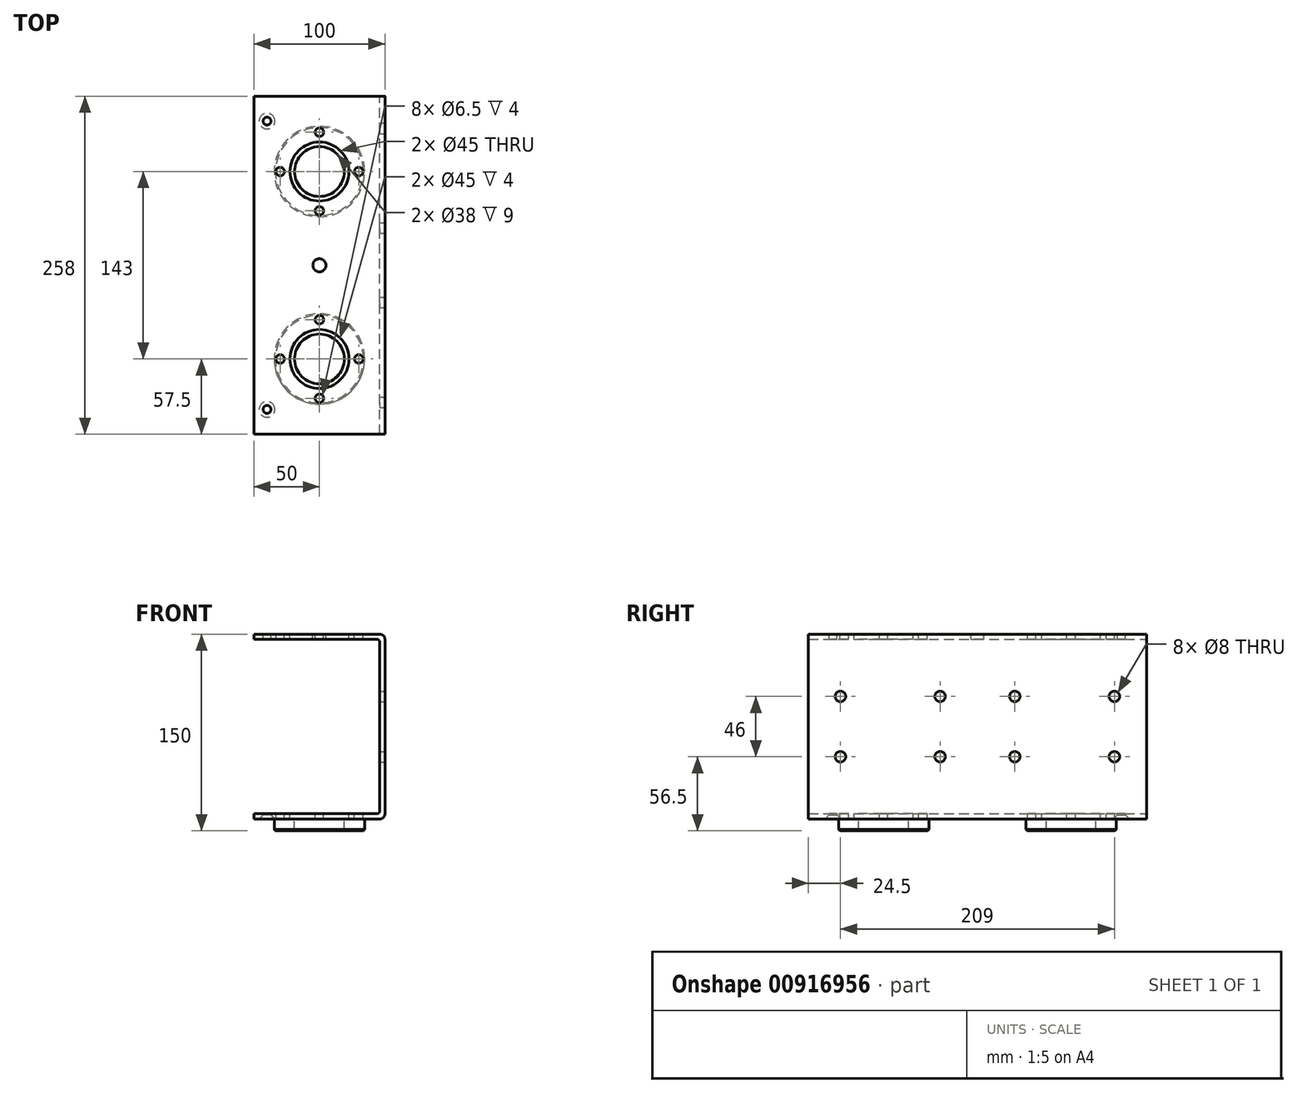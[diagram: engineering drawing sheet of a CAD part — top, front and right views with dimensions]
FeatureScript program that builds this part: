
annotation { "Feature Type Name" : "Feature", "Feature Type Description" : "" }
export const myFeature = defineFeature(function(context is Context, id is Id, definition is map)
    precondition{}
    {
        {
            var Q0;
            Q0=qCreatedBy(makeId("Front.planeOp"),FACE);
            var sketch = newSketch(context, id + "F0", { "sketchPlane" : qUnion([Q0])});
            skLineSegment(sketch, "E0.bottom", {"start": v(0, 0) * mm, "end": v(96, 0) * mm});
            skLineSegment(sketch, "E0.top", {"start": v(0, 141) * mm, "end": v(96, 141) * mm});
            skLineSegment(sketch, "E0.left", {"start": v(0, 0) * mm, "end": v(0, 4) * mm});
            skLineSegment(sketch, "E0.right", {"start": v(100, 4) * mm, "end": v(100, 137) * mm});
            skLineSegment(sketch, "E1.0", {"start": v(0, 137) * mm, "end": v(94, 137) * mm});
            skLineSegment(sketch, "E2.0", {"start": v(96, 6) * mm, "end": v(96, 135) * mm});
            skLineSegment(sketch, "E3.0", {"start": v(0, 4) * mm, "end": v(94, 4) * mm});
            skLineSegment(sketch, "E4.trimOffspring", {"start": v(0, 137) * mm, "end": v(0, 141) * mm});
            skPoint(sketch, "E5.visualSharp", {"position": v(100, 141) * mm});
            skArc(sketch, "E5.filletArc", {"start": v(100, 137) * mm, "mid": v(98.83, 139.83) * mm, "end": v(96, 141) * mm});
            skArc(sketch, "E6.filletArc", {"start": v(96, 135) * mm, "mid": v(95.41, 136.41) * mm, "end": v(94, 137) * mm});
            skPoint(sketch, "E7.visualSharp", {"position": v(96, 4) * mm});
            skArc(sketch, "E7.filletArc", {"start": v(94, 4) * mm, "mid": v(95.41, 4.59) * mm, "end": v(96, 6) * mm});
            skPoint(sketch, "E8.visualSharp", {"position": v(100, 0) * mm});
            skArc(sketch, "E8.filletArc", {"start": v(96, 0) * mm, "mid": v(98.83, 1.17) * mm, "end": v(100, 4) * mm});
            skSolve(sketch);
        }
        {
            var Q0;
            Q0 = qSketchRegion(id + "F0", true);
            extrude(context, id + "F1", {"entities" : qUnion([Q0]), "depth" : 258 * mm, "offsetDistance" : 25 * mm});
        }
        {
            var Q0;
            Q0=makeQuery(id+"F1.opExtrude","SWEPT_FACE",FACE,{"disambiguationData":[OSD([sQuery(id+"F0.wireOp",EDGE,"E0.top")])]});
            var sketch = newSketch(context, id + "F2", { "sketchPlane" : qUnion([Q0])});
            skCircle(sketch, "E9", {"center": v(50, -200.5) * mm, "radius": 22.5 * mm});
            skCircle(sketch, "E10", {"center": v(50, -57.5) * mm, "radius": 22.5 * mm});
            skCircle(sketch, "E11", {"center": v(50, -129) * mm, "radius": 5 * mm});
            skPoint(sketch, "E11.centerSnap0", {"position": v(0, -129) * mm});
            skCircle(sketch, "E12", {"center": v(50, -200.5) * mm, "radius": 30 * mm, "construction": true});
            skCircle(sketch, "E13", {"center": v(20, -200.5) * mm, "radius": 3.25 * mm});
            skCircle(sketch, "E14", {"center": v(80, -200.5) * mm, "radius": 3.25 * mm});
            skCircle(sketch, "E15", {"center": v(50, -170.5) * mm, "radius": 3.25 * mm});
            skCircle(sketch, "E16", {"center": v(50, -230.5) * mm, "radius": 3.25 * mm});
            skCircle(sketch, "E17.0.1.0", {"center": v(80, -57.5) * mm, "radius": 3.25 * mm});
            skCircle(sketch, "E17.0.1.1", {"center": v(50, -27.5) * mm, "radius": 3.25 * mm});
            skCircle(sketch, "E17.0.1.2", {"center": v(20, -57.5) * mm, "radius": 3.25 * mm});
            skCircle(sketch, "E17.0.1.3", {"center": v(50, -87.5) * mm, "radius": 3.25 * mm});
            skLineSegment(sketch, "E17.direction1", {"start": v(80, -200.5) * mm, "end": v(105, -200.5) * mm, "construction": true});
            skLineSegment(sketch, "E17.direction2", {"start": v(80, -200.5) * mm, "end": v(80, -57.5) * mm, "construction": true});
            skSolve(sketch);
        }
        {
            var Q0;
            Q0=makeQuery(id+"F2.imprint","IMPRINT",FACE,{"disambiguationData":[TD([[makeQuery(id+"F2.imprint","IMPRINT",EDGE,{"derivedFrom":sQuery(id+"F2.wireOp",EDGE,"E9")}),1.0]])]});
            var Q1;
            Q1=makeQuery(id+"F2.imprint","IMPRINT",FACE,{"disambiguationData":[TD([[makeQuery(id+"F2.imprint","IMPRINT",EDGE,{"derivedFrom":sQuery(id+"F2.wireOp",EDGE,"E17.0.1.3")}),1.0]])]});
            var Q2;
            Q2=makeQuery(id+"F2.imprint","IMPRINT",FACE,{"disambiguationData":[TD([[makeQuery(id+"F2.imprint","IMPRINT",EDGE,{"derivedFrom":sQuery(id+"F2.wireOp",EDGE,"E10")}),1.0]])]});
            var Q3;
            Q3=makeQuery(id+"F2.imprint","IMPRINT",FACE,{"disambiguationData":[TD([[makeQuery(id+"F2.imprint","IMPRINT",EDGE,{"derivedFrom":sQuery(id+"F2.wireOp",EDGE,"E17.0.1.2")}),1.0]])]});
            var Q4;
            Q4=makeQuery(id+"F2.imprint","IMPRINT",FACE,{"disambiguationData":[TD([[makeQuery(id+"F2.imprint","IMPRINT",EDGE,{"derivedFrom":sQuery(id+"F2.wireOp",EDGE,"E17.0.1.0")}),1.0]])]});
            var Q5;
            Q5=makeQuery(id+"F2.imprint","IMPRINT",FACE,{"disambiguationData":[TD([[makeQuery(id+"F2.imprint","IMPRINT",EDGE,{"derivedFrom":sQuery(id+"F2.wireOp",EDGE,"E17.0.1.1")}),1.0]])]});
            var Q6;
            Q6=makeQuery(id+"F2.imprint","IMPRINT",FACE,{"disambiguationData":[TD([[makeQuery(id+"F2.imprint","IMPRINT",EDGE,{"derivedFrom":sQuery(id+"F2.wireOp",EDGE,"E15")}),1.0]])]});
            var Q7;
            Q7=makeQuery(id+"F2.imprint","IMPRINT",FACE,{"disambiguationData":[TD([[makeQuery(id+"F2.imprint","IMPRINT",EDGE,{"derivedFrom":sQuery(id+"F2.wireOp",EDGE,"E14")}),1.0]])]});
            var Q8;
            Q8=makeQuery(id+"F2.imprint","IMPRINT",FACE,{"disambiguationData":[TD([[makeQuery(id+"F2.imprint","IMPRINT",EDGE,{"derivedFrom":sQuery(id+"F2.wireOp",EDGE,"E16")}),1.0]])]});
            var Q9;
            Q9=makeQuery(id+"F2.imprint","IMPRINT",FACE,{"disambiguationData":[TD([[makeQuery(id+"F2.imprint","IMPRINT",EDGE,{"derivedFrom":sQuery(id+"F2.wireOp",EDGE,"E13")}),1.0]])]});
            extrude(context, id + "F3", {"entities" : qUnion([Q0, Q1, Q2, Q3, Q4, Q5, Q6, Q7, Q8, Q9]), "operationType" : NewBodyOperationType.REMOVE, "endBound" : BoundingType.THROUGH_ALL, "oppositeDirection" : true, "depth" : 25 * mm, "offsetDistance" : 25 * mm});
        }
        {
            var Q0;
            Q0=makeQuery(id+"F2.imprint","IMPRINT",FACE,{"disambiguationData":[TD([[makeQuery(id+"F2.imprint","IMPRINT",EDGE,{"derivedFrom":sQuery(id+"F2.wireOp",EDGE,"E11")}),1.0]])]});
            extrude(context, id + "F4", {"entities" : qUnion([Q0]), "operationType" : NewBodyOperationType.REMOVE, "endBound" : BoundingType.UP_TO_NEXT, "oppositeDirection" : true, "depth" : 25 * mm, "offsetDistance" : 25 * mm});
        }
        {
            var Q0;
            Q0=makeQuery(id+"F1.opExtrude","SWEPT_FACE",FACE,{"disambiguationData":[OSD([sQuery(id+"F0.wireOp",EDGE,"E0.right")])]});
            var sketch = newSketch(context, id + "F5", { "sketchPlane" : qUnion([Q0])});
            skCircle(sketch, "E18", {"center": v(-233.5, 93.5) * mm, "radius": 4 * mm});
            skCircle(sketch, "E19.0.1.0", {"center": v(-233.5, 47.5) * mm, "radius": 4 * mm});
            skCircle(sketch, "E19.1.0.0", {"center": v(-157.5, 93.5) * mm, "radius": 4 * mm});
            skCircle(sketch, "E19.1.1.0", {"center": v(-157.5, 47.5) * mm, "radius": 4 * mm});
            skLineSegment(sketch, "E19.direction1", {"start": v(-233.5, 93.5) * mm, "end": v(-157.5, 93.5) * mm, "construction": true});
            skLineSegment(sketch, "E19.direction2", {"start": v(-233.5, 93.5) * mm, "end": v(-233.5, 47.5) * mm, "construction": true});
            skLineSegment(sketch, "E20", {"start": v(-129, 137) * mm, "end": v(-129, 116.07) * mm, "construction": true});
            skCircle(sketch, "E21.MirrorC", {"center": v(-100.5, 93.5) * mm, "radius": 4 * mm});
            skCircle(sketch, "E22.MirrorC", {"center": v(-100.5, 47.5) * mm, "radius": 4 * mm});
            skCircle(sketch, "E23.MirrorC", {"center": v(-24.5, 93.5) * mm, "radius": 4 * mm});
            skCircle(sketch, "E24.MirrorC", {"center": v(-24.5, 47.5) * mm, "radius": 4 * mm});
            skSolve(sketch);
        }
        {
            var Q0;
            Q0 = qSketchRegion(id + "F5", true);
            extrude(context, id + "F6", {"entities" : qUnion([Q0]), "operationType" : NewBodyOperationType.REMOVE, "endBound" : BoundingType.THROUGH_ALL, "oppositeDirection" : true, "depth" : 25 * mm, "offsetDistance" : 25 * mm});
        }
        {
            var Q0;
            Q0=makeQuery(id+"F1.opExtrude","SWEPT_FACE",FACE,{"disambiguationData":[OSD([sQuery(id+"F0.wireOp",EDGE,"E0.top")])]});
            var sketch = newSketch(context, id + "F7", { "sketchPlane" : qUnion([Q0])});
            skCircle(sketch, "E25", {"center": v(10, -239) * mm, "radius": 3 * mm});
            skLineSegment(sketch, "E26", {"start": v(0, -129) * mm, "end": v(-19.63, -129) * mm, "construction": true});
            skCircle(sketch, "E27.MirrorC", {"center": v(10, -19) * mm, "radius": 3 * mm});
            skSolve(sketch);
        }
        {
            var Q0;
            Q0 = qSketchRegion(id + "F7", true);
            extrude(context, id + "F8", {"entities" : qUnion([Q0]), "operationType" : NewBodyOperationType.REMOVE, "endBound" : BoundingType.THROUGH_ALL, "oppositeDirection" : true, "depth" : 25 * mm, "offsetDistance" : 25 * mm});
        }
        {
            var Q0;
            Q0=makeQuery(id+"F8.boolean.opBoolean","COPY",EDGE,{"derivedFrom":makeQuery(id+"F8.opExtrude","CAP_EDGE",EDGE,{"disambiguationData":[OSD([sQuery(id+"F7.wireOp",EDGE,"E27.MirrorC")])],"isStart":true})});
            var Q1;
            Q1=makeQuery(id+"F8.boolean.opBoolean","COPY",EDGE,{"derivedFrom":makeQuery(id+"F8.opExtrude","CAP_EDGE",EDGE,{"disambiguationData":[OSD([sQuery(id+"F7.wireOp",EDGE,"E25")])],"isStart":true})});
            var Q2;
            Q2=makeQuery(id+"F8.boolean.opBoolean","INTERSECT",EDGE,{"derivedFrom":[makeQuery(id+"F1.opExtrude","SWEPT_FACE",FACE,{"disambiguationData":[OSD([sQuery(id+"F0.wireOp",EDGE,"E0.bottom")])]}),makeQuery(id+"F8.opExtrude","SWEPT_FACE",FACE,{"disambiguationData":[OSD([sQuery(id+"F7.wireOp",EDGE,"E25")])]})]});
            var Q3;
            Q3=makeQuery(id+"F8.boolean.opBoolean","INTERSECT",EDGE,{"derivedFrom":[makeQuery(id+"F1.opExtrude","SWEPT_FACE",FACE,{"disambiguationData":[OSD([sQuery(id+"F0.wireOp",EDGE,"E0.bottom")])]}),makeQuery(id+"F8.opExtrude","SWEPT_FACE",FACE,{"disambiguationData":[OSD([sQuery(id+"F7.wireOp",EDGE,"E27.MirrorC")])]})]});
            chamfer(context, id + "F9", {"entities" : qUnion([Q0, Q1, Q2, Q3]), "chamferType" : ChamferType.TWO_OFFSETS, "width1" : 3 * mm, "oppositeDirection" : false, "width2" : 3 * mm, "tangentPropagation" : true});
        }
        {
            var Q0;
            Q0=makeQuery(id+"F1.opExtrude","SWEPT_FACE",FACE,{"disambiguationData":[OSD([sQuery(id+"F0.wireOp",EDGE,"E0.bottom")])]});
            var sketch = newSketch(context, id + "F10", { "sketchPlane" : qUnion([Q0])});
            skCircle(sketch, "E28", {"center": v(50, 57.5) * mm, "radius": 34.5 * mm});
            skCircle(sketch, "E29", {"center": v(50, 200.5) * mm, "radius": 34.5 * mm});
            skCircle(sketch, "E30", {"center": v(50, 200.5) * mm, "radius": 19 * mm});
            skCircle(sketch, "E31", {"center": v(50, 57.5) * mm, "radius": 19 * mm});
            skSolve(sketch);
        }
        {
            var Q0;
            Q0 = qSketchRegion(id + "F10", true);
            extrude(context, id + "F11", {"entities" : qUnion([Q0]), "operationType" : NewBodyOperationType.ADD, "depth" : 9 * mm, "offsetDistance" : 25 * mm});
        }
        {
            var Q0;
            Q0=makeQuery(id+"F11.opExtrude","CAP_EDGE",EDGE,{"disambiguationData":[OSD([sQuery(id+"F10.wireOp",EDGE,"E29")])],"isStart":false});
            var Q1;
            Q1=makeQuery(id+"F11.opExtrude","CAP_EDGE",EDGE,{"disambiguationData":[OSD([sQuery(id+"F10.wireOp",EDGE,"E28")])],"isStart":false});
            chamfer(context, id + "F12", {"entities" : qUnion([Q0, Q1]), "width" : 1 * mm, "tangentPropagation" : true});
        }
    });
